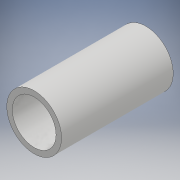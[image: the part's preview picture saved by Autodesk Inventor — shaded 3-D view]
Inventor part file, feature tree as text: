
AUTODESK INVENTOR PART (.ipt)
format: ipt  version: 2018.2 (Build 222227000, 227)  size: 99,840 bytes
history: native  units: mm
features: other x1, extrude x1, sketch x1
ambient origin geometry x8: Origin, YZ Plane, XZ Plane, XY Plane, X Axis, Y Axis, Z Axis, Center Point
bodies: Body1 (feature_tree)
feature tree (3):
  other  "ソリッド1"
  extrude  "押し出し1"  Depth=10.0mm
  sketch  "スケッチ1"
